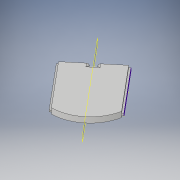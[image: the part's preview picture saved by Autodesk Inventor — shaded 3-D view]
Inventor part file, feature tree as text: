
AUTODESK INVENTOR PART (.ipt)
format: ipt  version: 2019 (Build 230136000, 136)  size: 171,008 bytes
history: native  units: in
note: dims shown in document units (in); Inventor stores cm internally (conversion verified against a paired STEP export)
features: fillet x6, sketch x5, extrude x3, plane x1, mirror x1, chamfer x1
ambient origin geometry x8: Origin, YZ Plane, XZ Plane, XY Plane, X Axis, Y Axis, Z Axis, Center Point
bodies: Solid1 (feature_tree)
feature tree (17):
  extrude  "Extrusion1"  Depth=2.475in
  extrude  "Extrusion2"  Depth=0.27in TaperAngle=0.0deg
  plane  "Work Plane1"
  mirror  "Mirror1"
  extrude  "Extrusion3"  Depth=0.1in
  chamfer  "Chamfer1"  Distance=0.08in
  fillet  "Fillet1"  Radius=0.15in
  fillet  "Fillet2"  Radius=0.15in
  fillet  "Fillet3"  Radius=0.15in
  fillet  "Fillet4"  Radius=0.1in
  fillet  "Fillet5"  Radius=0.125in
  fillet  "Fillet6"  Radius=0.125in
  sketch  "Sketch4"  dims[d14=0.1in d15=0.125in d16=45.0deg d17=0.125in d18=0.125in]
  sketch  "Sketch5"  dims[d19=0.1in d20=0.1in d21=0.1in d22=0.1in]
  sketch  "Sketch1"  dims[d0=3.937in d1=2.475in]
  sketch  "Sketch2"  dims[d2=2.8165in d3=0.27in d4=0.0in]
  sketch  "Sketch3"  dims[d5=0.085in d6=0.085in d7=0.08in d8=0.0in d9=0.15in d10=0.15in d11=0.15in d12=0.1in d13=0.0in]
